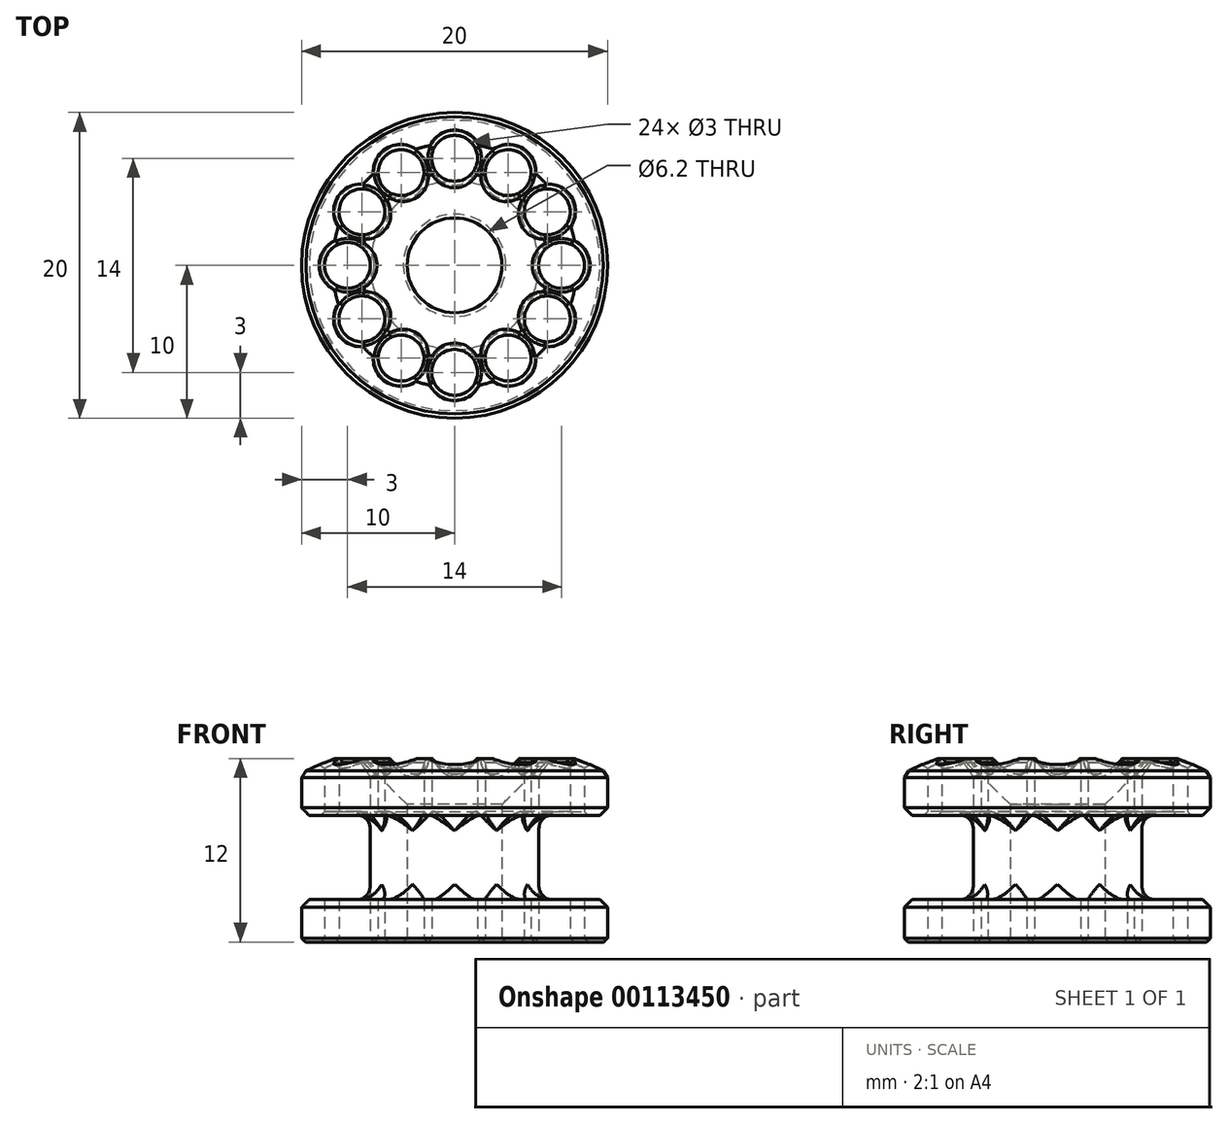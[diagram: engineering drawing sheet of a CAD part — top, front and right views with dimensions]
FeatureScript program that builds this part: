
annotation { "Feature Type Name" : "Feature", "Feature Type Description" : "" }
export const myFeature = defineFeature(function(context is Context, id is Id, definition is map)
    precondition{}
    {
        {
            var Q0;
            Q0=qCreatedBy(makeId("Top.planeOp"),FACE);
            var sketch = newSketch(context, id + "F0", { "sketchPlane" : qUnion([Q0])});
            skCircle(sketch, "E0", {"center": v(0, 0) * mm, "radius": 3.1 * mm});
            skCircle(sketch, "E1", {"center": v(0, 0) * mm, "radius": 10 * mm});
            skLineSegment(sketch, "E2", {"start": v(0, 10) * mm, "end": v(0, 4) * mm, "construction": true});
            skCircle(sketch, "E3", {"center": v(0, 7) * mm, "radius": 1.5 * mm});
            skCircle(sketch, "E4.1.0", {"center": v(-3.5, 6.06) * mm, "radius": 1.5 * mm});
            skCircle(sketch, "E4.2.0", {"center": v(-6.06, 3.5) * mm, "radius": 1.5 * mm});
            skCircle(sketch, "E4.3.0", {"center": v(-7, 0) * mm, "radius": 1.5 * mm});
            skCircle(sketch, "E4.4.0", {"center": v(-6.06, -3.5) * mm, "radius": 1.5 * mm});
            skCircle(sketch, "E4.5.0", {"center": v(-3.5, -6.06) * mm, "radius": 1.5 * mm});
            skCircle(sketch, "E4.6.0", {"center": v(0, -7) * mm, "radius": 1.5 * mm});
            skCircle(sketch, "E4.7.0", {"center": v(3.5, -6.06) * mm, "radius": 1.5 * mm});
            skCircle(sketch, "E4.8.0", {"center": v(6.06, -3.5) * mm, "radius": 1.5 * mm});
            skCircle(sketch, "E4.9.0", {"center": v(7, 0) * mm, "radius": 1.5 * mm});
            skCircle(sketch, "E4.10.0", {"center": v(6.06, 3.5) * mm, "radius": 1.5 * mm});
            skCircle(sketch, "E4.11.0", {"center": v(3.5, 6.06) * mm, "radius": 1.5 * mm});
            skSolve(sketch);
        }
        {
            var Q0;
            Q0=makeQuery(id+"F0.imprint","IMPRINT",FACE,{"disambiguationData":[TD([[makeQuery(id+"F0.imprint","IMPRINT",EDGE,{"derivedFrom":sQuery(id+"F0.wireOp",EDGE,"E0")}),-1.0]])]});
            extrude(context, id + "F1", {"entities" : qUnion([Q0]), "depth" : 12 * mm});
        }
        {
            var Q0;
            Q0=makeQuery(id+"F1.opExtrude","CAP_EDGE",EDGE,{"disambiguationData":[OSD([sQuery(id+"F0.wireOp",EDGE,"E0")])],"isStart":false});
            chamfer(context, id + "F2", {"entities" : qUnion([Q0]), "width" : 3 * mm});
        }
        {
            var Q0;
            Q0=makeQuery(id+"F1.opExtrude","CAP_EDGE",EDGE,{"disambiguationData":[OSD([sQuery(id+"F0.wireOp",EDGE,"E1")])],"isStart":false});
            chamfer(context, id + "F3", {"entities" : qUnion([Q0]), "chamferType" : ChamferType.OFFSET_ANGLE, "width" : 2 * mm, "oppositeDirection" : false, "angle" : 25 * degree, "tangentPropagation" : true});
        }
        {
            var Q0;
            Q0=qCreatedBy(makeId("Right.planeOp"),FACE);
            var sketch = newSketch(context, id + "F4", { "sketchPlane" : qUnion([Q0])});
            skLineSegment(sketch, "E5.0", {"start": v(10, 11.07) * mm, "end": v(-10, 11.07) * mm});
            skLineSegment(sketch, "E6", {"start": v(10, 11.07) * mm, "end": v(10, 0) * mm, "construction": true});
            skLineSegment(sketch, "E7.bottom", {"start": v(6.5, 8.28) * mm, "end": v(14.5, 8.28) * mm});
            skLineSegment(sketch, "E7.top", {"start": v(6.5, 2.78) * mm, "end": v(14.5, 2.78) * mm});
            skLineSegment(sketch, "E7.left", {"start": v(5.5, 7.28) * mm, "end": v(5.5, 3.78) * mm});
            skLineSegment(sketch, "E7.right", {"start": v(14.5, 8.28) * mm, "end": v(14.5, 2.78) * mm});
            skPoint(sketch, "E7.middle", {"position": v(10, 5.53) * mm});
            skPoint(sketch, "E8.visualSharp", {"position": v(5.5, 2.78) * mm});
            skArc(sketch, "E8.filletArc", {"start": v(5.5, 3.78) * mm, "mid": v(5.8, 3.08) * mm, "end": v(6.5, 2.78) * mm});
            skPoint(sketch, "E9.visualSharp", {"position": v(5.5, 8.28) * mm});
            skArc(sketch, "E9.filletArc", {"start": v(6.5, 8.28) * mm, "mid": v(5.8, 8) * mm, "end": v(5.5, 7.28) * mm});
            skSolve(sketch);
        }
        {
            var Q0;
            Q0=makeQuery(id+"F4.imprint","IMPRINT",FACE,{"disambiguationData":[TD([[makeQuery(id+"F4.imprint","IMPRINT",EDGE,{"derivedFrom":sQuery(id+"F4.wireOp",EDGE,"E7.bottom")}),-1.0]])]});
            var Q1;
            Q1=makeQuery(id+"F1.opExtrude","SWEPT_FACE",FACE,{"disambiguationData":[OSD([sQuery(id+"F0.wireOp",EDGE,"E1")])]});
            revolve(context, id + "F5", {"operationType" : NewBodyOperationType.REMOVE, "entities" : qUnion([Q0]), "axis" : qUnion([Q1]), "revolveType" : RevolveType.FULL, "oppositeDirection" : true});
        }
        {
            var Q0;
            Q0=makeQuery(id+"F5.boolean.opBoolean","INTERSECT",EDGE,{"derivedFrom":[makeQuery(id+"F1.opExtrude","SWEPT_FACE",FACE,{"disambiguationData":[OSD([sQuery(id+"F0.wireOp",EDGE,"E1")])]}),makeQuery(id+"F5.opRevolve","SWEPT_FACE",FACE,{"disambiguationData":[OSD([sQuery(id+"F4.wireOp",EDGE,"E7.bottom")])]})]});
            var Q1;
            Q1=makeQuery(id+"F5.boolean.opBoolean","INTERSECT",EDGE,{"derivedFrom":[makeQuery(id+"F1.opExtrude","SWEPT_FACE",FACE,{"disambiguationData":[OSD([sQuery(id+"F0.wireOp",EDGE,"E1")])]}),makeQuery(id+"F5.opRevolve","SWEPT_FACE",FACE,{"disambiguationData":[OSD([sQuery(id+"F4.wireOp",EDGE,"E7.top")])]})]});
            var Q2;
            {var subQ0=sQuery(id+"F0.wireOp",EDGE,"E1");Q2=makeQuery(id+"F3.opChamfer","BLEND_EDGE",EDGE,{"blendedFrom":[makeQuery(id+"F1.opExtrude","CAP_EDGE",EDGE,{"disambiguationData":[OSD([subQ0])],"isStart":false}),makeQuery(id+"F1.opExtrude","SWEPT_FACE",FACE,{"disambiguationData":[OSD([subQ0])]})],"blendedInto":[makeQuery(id+"F1.opExtrude","SWEPT_FACE",FACE,{"disambiguationData":[OSD([subQ0])]})]});}
            chamfer(context, id + "F6", {"entities" : qUnion([Q0, Q1, Q2]), "width" : .5 * mm, "tangentPropagation" : true});
        }
        {
            var Q0;
            {var subQ0=sQuery(id+"F0.wireOp",EDGE,"E4.7.0");var subQ1=sQuery(id+"F0.wireOp",EDGE,"E1");Q0=makeQuery(id+"F5.boolean.opBoolean","SPLIT",FACE,{"disambiguationData":[TD([makeQuery(id+"F3.opChamfer","BLEND_FACE",FACE,{"disambiguationData":[OSD([subQ1])]})])],"derivedFrom":makeQuery(id+"F1.opExtrude","SWEPT_FACE",FACE,{"disambiguationData":[OSD([subQ0])]})});}
            var Q1;
            {var subQ0=sQuery(id+"F0.wireOp",EDGE,"E4.8.0");var subQ1=sQuery(id+"F0.wireOp",EDGE,"E1");Q1=makeQuery(id+"F5.boolean.opBoolean","SPLIT",FACE,{"disambiguationData":[TD([makeQuery(id+"F3.opChamfer","BLEND_FACE",FACE,{"disambiguationData":[OSD([subQ1])]})])],"derivedFrom":makeQuery(id+"F1.opExtrude","SWEPT_FACE",FACE,{"disambiguationData":[OSD([subQ0])]})});}
            var Q2;
            {var subQ0=sQuery(id+"F0.wireOp",EDGE,"E4.9.0");var subQ1=sQuery(id+"F0.wireOp",EDGE,"E1");Q2=makeQuery(id+"F5.boolean.opBoolean","SPLIT",FACE,{"disambiguationData":[TD([makeQuery(id+"F3.opChamfer","BLEND_FACE",FACE,{"disambiguationData":[OSD([subQ1])]})])],"derivedFrom":makeQuery(id+"F1.opExtrude","SWEPT_FACE",FACE,{"disambiguationData":[OSD([subQ0])]})});}
            var Q3;
            {var subQ0=sQuery(id+"F0.wireOp",EDGE,"E4.10.0");var subQ1=sQuery(id+"F0.wireOp",EDGE,"E1");Q3=makeQuery(id+"F5.boolean.opBoolean","SPLIT",FACE,{"disambiguationData":[TD([makeQuery(id+"F3.opChamfer","BLEND_FACE",FACE,{"disambiguationData":[OSD([subQ1])]})])],"derivedFrom":makeQuery(id+"F1.opExtrude","SWEPT_FACE",FACE,{"disambiguationData":[OSD([subQ0])]})});}
            var Q4;
            {var subQ0=sQuery(id+"F0.wireOp",EDGE,"E4.11.0");var subQ1=sQuery(id+"F0.wireOp",EDGE,"E1");Q4=makeQuery(id+"F5.boolean.opBoolean","SPLIT",FACE,{"disambiguationData":[TD([makeQuery(id+"F3.opChamfer","BLEND_FACE",FACE,{"disambiguationData":[OSD([subQ1])]})])],"derivedFrom":makeQuery(id+"F1.opExtrude","SWEPT_FACE",FACE,{"disambiguationData":[OSD([subQ0])]})});}
            var Q5;
            {var subQ0=sQuery(id+"F0.wireOp",EDGE,"E3");var subQ1=sQuery(id+"F0.wireOp",EDGE,"E1");Q5=makeQuery(id+"F5.boolean.opBoolean","SPLIT",FACE,{"disambiguationData":[TD([makeQuery(id+"F3.opChamfer","BLEND_FACE",FACE,{"disambiguationData":[OSD([subQ1])]})])],"derivedFrom":makeQuery(id+"F1.opExtrude","SWEPT_FACE",FACE,{"disambiguationData":[OSD([subQ0])]})});}
            var Q6;
            {var subQ0=sQuery(id+"F0.wireOp",EDGE,"E4.1.0");var subQ1=sQuery(id+"F0.wireOp",EDGE,"E1");Q6=makeQuery(id+"F5.boolean.opBoolean","SPLIT",FACE,{"disambiguationData":[TD([makeQuery(id+"F3.opChamfer","BLEND_FACE",FACE,{"disambiguationData":[OSD([subQ1])]})])],"derivedFrom":makeQuery(id+"F1.opExtrude","SWEPT_FACE",FACE,{"disambiguationData":[OSD([subQ0])]})});}
            var Q7;
            {var subQ0=sQuery(id+"F0.wireOp",EDGE,"E4.3.0");var subQ1=sQuery(id+"F0.wireOp",EDGE,"E1");Q7=makeQuery(id+"F5.boolean.opBoolean","SPLIT",FACE,{"disambiguationData":[TD([makeQuery(id+"F3.opChamfer","BLEND_FACE",FACE,{"disambiguationData":[OSD([subQ1])]})])],"derivedFrom":makeQuery(id+"F1.opExtrude","SWEPT_FACE",FACE,{"disambiguationData":[OSD([subQ0])]})});}
            var Q8;
            {var subQ0=sQuery(id+"F0.wireOp",EDGE,"E4.4.0");var subQ1=sQuery(id+"F0.wireOp",EDGE,"E1");Q8=makeQuery(id+"F5.boolean.opBoolean","SPLIT",FACE,{"disambiguationData":[TD([makeQuery(id+"F3.opChamfer","BLEND_FACE",FACE,{"disambiguationData":[OSD([subQ1])]})])],"derivedFrom":makeQuery(id+"F1.opExtrude","SWEPT_FACE",FACE,{"disambiguationData":[OSD([subQ0])]})});}
            var Q9;
            {var subQ0=sQuery(id+"F0.wireOp",EDGE,"E4.5.0");var subQ1=sQuery(id+"F0.wireOp",EDGE,"E1");Q9=makeQuery(id+"F5.boolean.opBoolean","SPLIT",FACE,{"disambiguationData":[TD([makeQuery(id+"F3.opChamfer","BLEND_FACE",FACE,{"disambiguationData":[OSD([subQ1])]})])],"derivedFrom":makeQuery(id+"F1.opExtrude","SWEPT_FACE",FACE,{"disambiguationData":[OSD([subQ0])]})});}
            var Q10;
            {var subQ0=sQuery(id+"F0.wireOp",EDGE,"E4.6.0");var subQ1=sQuery(id+"F0.wireOp",EDGE,"E1");Q10=makeQuery(id+"F5.boolean.opBoolean","SPLIT",FACE,{"disambiguationData":[TD([makeQuery(id+"F3.opChamfer","BLEND_FACE",FACE,{"disambiguationData":[OSD([subQ1])]})])],"derivedFrom":makeQuery(id+"F1.opExtrude","SWEPT_FACE",FACE,{"disambiguationData":[OSD([subQ0])]})});}
            var Q11;
            {var subQ0=sQuery(id+"F0.wireOp",EDGE,"E4.2.0");var subQ1=sQuery(id+"F0.wireOp",EDGE,"E1");Q11=makeQuery(id+"F5.boolean.opBoolean","SPLIT",FACE,{"disambiguationData":[TD([makeQuery(id+"F3.opChamfer","BLEND_FACE",FACE,{"disambiguationData":[OSD([subQ1])]})])],"derivedFrom":makeQuery(id+"F1.opExtrude","SWEPT_FACE",FACE,{"disambiguationData":[OSD([subQ0])]})});}
            var Q12;
            Q12=makeQuery(id+"F1.opExtrude","CAP_FACE",FACE,{"disambiguationData":[OSD([sQuery(id+"F0.wireOp",EDGE,"E0"),sQuery(id+"F0.wireOp",EDGE,"E1"),sQuery(id+"F0.wireOp",EDGE,"E3"),sQuery(id+"F0.wireOp",EDGE,"E4.1.0"),sQuery(id+"F0.wireOp",EDGE,"E4.2.0"),sQuery(id+"F0.wireOp",EDGE,"E4.3.0"),sQuery(id+"F0.wireOp",EDGE,"E4.4.0"),sQuery(id+"F0.wireOp",EDGE,"E4.5.0"),sQuery(id+"F0.wireOp",EDGE,"E4.6.0"),sQuery(id+"F0.wireOp",EDGE,"E4.7.0"),sQuery(id+"F0.wireOp",EDGE,"E4.8.0"),sQuery(id+"F0.wireOp",EDGE,"E4.9.0"),sQuery(id+"F0.wireOp",EDGE,"E4.10.0"),sQuery(id+"F0.wireOp",EDGE,"E4.11.0")])],"isStart":true});
            chamfer(context, id + "F7", {"entities" : qUnion([Q0, Q1, Q2, Q3, Q4, Q5, Q6, Q7, Q8, Q9, Q10, Q11, Q12]), "width" : .25 * mm, "tangentPropagation" : true});
        }
    });
